# Revit family: FN1
name_source: partatom
category: Lighting Fixtures
units: mm (PartAtom-declared; Revit-internal decimal feet)

## family parameters
Cut with Voids When Loaded = No
Host = Face
Light Source = Yes
OmniClass Number = 23.80.70.14.14
OmniClass Title = Exterior Floodlights
Part Type = Normal
Room Calculation Point = No
Round Connector Dimension = Use Diameter
Shared = Yes

## types (2) — shared parameters
Apparent Load = 25 VA
Assembly Code = D5020200
Certifications = UL,CSA,Wet Listed
Color Filter = 16777215
Connector Description = Lighting Connector
Default Elevation = 48 "
Description = Fresno Bollards
Dimming Lamp Color Temperature Shift = <None>
Features = 30w and 46w energy-efficient LED systems
Extruded aluminum square or round housing, with tamper resistant hardware. Flat top, or optional dome top for round FN2. Single screw access for top relamping.
Sealed one-piece, clear acrylic lens
Specular, anodized aluminum optical systems
Housing Material = Paint - Carbon Black
Lamp = LED
Length = 48 "
Load Classification = Lighting
Manufacturer = Securitylighting
Power Factor = 1
Reflector Finish = White Glass
Source = Steel_Galvanized
Tilt Angle = 60.00°
URL = https://www.currentlighting.com
Voltage = 120 V
Warranty = 5 years Warranty
Wattage Comments = 25W
Watts = 25 W
Width = 11.63 "
Width 1 = 5 "

## per-type parameters (varying)
| type | FN1 | FN2 | Photometric Web File |
| FN2 | No | Yes | FN2-12LU-4K-XX.ies |
| FN1 | Yes | No | FN1-12LU-3K-XX (1).ies |

note: column(s) folded — value = type name in every type: Model

## geometry (parser evidence)
native form markers: Sweep x5
no freeform markers — native parametric forms only
